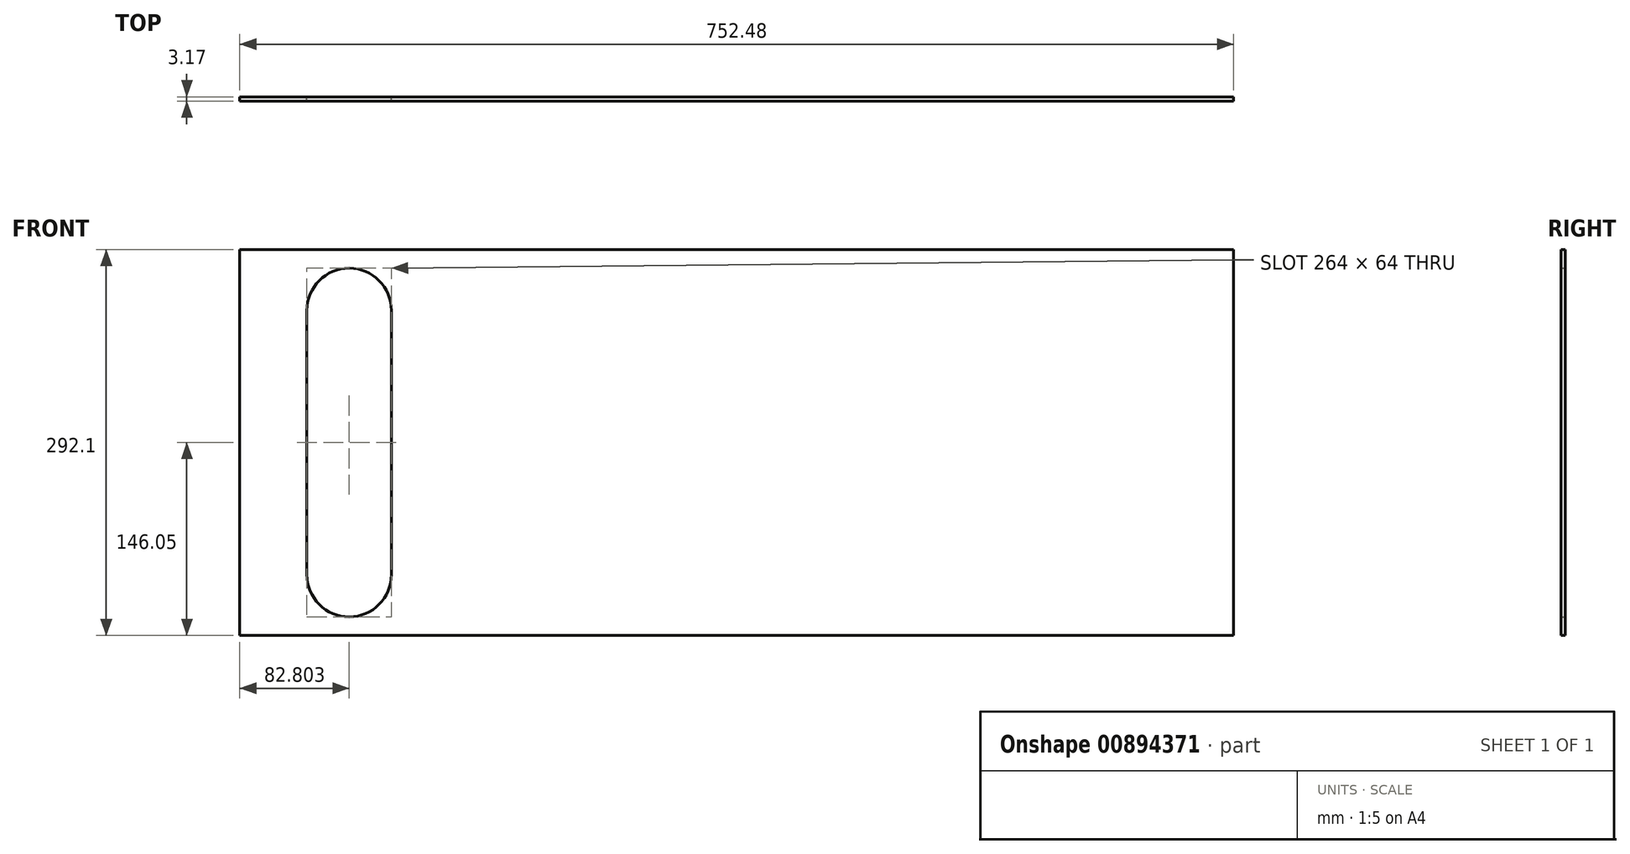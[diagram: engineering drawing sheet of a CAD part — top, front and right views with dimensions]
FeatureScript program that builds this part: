
annotation { "Feature Type Name" : "Feature", "Feature Type Description" : "" }
export const myFeature = defineFeature(function(context is Context, id is Id, definition is map)
    precondition{}
    {
        {
            var Q0;
            Q0=qCreatedBy(makeId("Front.planeOp"),FACE);
            var sketch = newSketch(context, id + "F0", { "sketchPlane" : qUnion([Q0])});
            skLineSegment(sketch, "E0.bottom", {"start": v(376.24, 146.05) * mm, "end": v(-376.24, 146.05) * mm});
            skLineSegment(sketch, "E0.top", {"start": v(376.24, -146.05) * mm, "end": v(-376.24, -146.05) * mm});
            skLineSegment(sketch, "E0.left", {"start": v(376.24, 146.05) * mm, "end": v(376.24, -146.05) * mm});
            skLineSegment(sketch, "E0.right", {"start": v(-376.24, 146.05) * mm, "end": v(-376.24, -146.05) * mm});
            skPoint(sketch, "E0.middle", {"position": v(0, 0) * mm});
            skLineSegment(sketch, "E1.bottom", {"start": v(-261.44, 100) * mm, "end": v(-325.44, 100) * mm, "construction": true});
            skLineSegment(sketch, "E1.top", {"start": v(-261.44, -100) * mm, "end": v(-325.44, -100) * mm, "construction": true});
            skLineSegment(sketch, "E1.left", {"start": v(-261.44, 100) * mm, "end": v(-261.44, -100) * mm});
            skLineSegment(sketch, "E1.right", {"start": v(-325.44, 100) * mm, "end": v(-325.44, -100) * mm});
            skPoint(sketch, "E1.middle", {"position": v(-293.44, 0) * mm});
            skLineSegment(sketch, "E2", {"start": v(-293.44, 0) * mm, "end": v(-376.24, 0) * mm, "construction": true});
            skArc(sketch, "E3", {"start": v(-325.44, 100) * mm, "mid": v(-293.44, 132) * mm, "end": v(-261.44, 100) * mm});
            skArc(sketch, "E4", {"start": v(-325.44, -100) * mm, "mid": v(-293.44, -132) * mm, "end": v(-261.44, -100) * mm});
            skSolve(sketch);
        }
        {
            var Q0;
            Q0=makeQuery(id+"F0.imprint","IMPRINT",FACE,{"disambiguationData":[TD([[makeQuery(id+"F0.imprint","IMPRINT",EDGE,{"derivedFrom":sQuery(id+"F0.wireOp",EDGE,"E0.bottom")}),1.0]])]});
            var Q1;
            Q1=sQuery(id+"F0.wireOp",EDGE,"E1.top");
            var Q2;
            Q2=sQuery(id+"F0.wireOp",EDGE,"E1.bottom");
            extrude(context, id + "F1", {"entities" : qUnion([Q0]), "surfaceEntities" : qUnion([Q1, Q2]), "depth" : 3.17 * mm, "offsetDistance" : 25.4 * mm});
        }
    });
